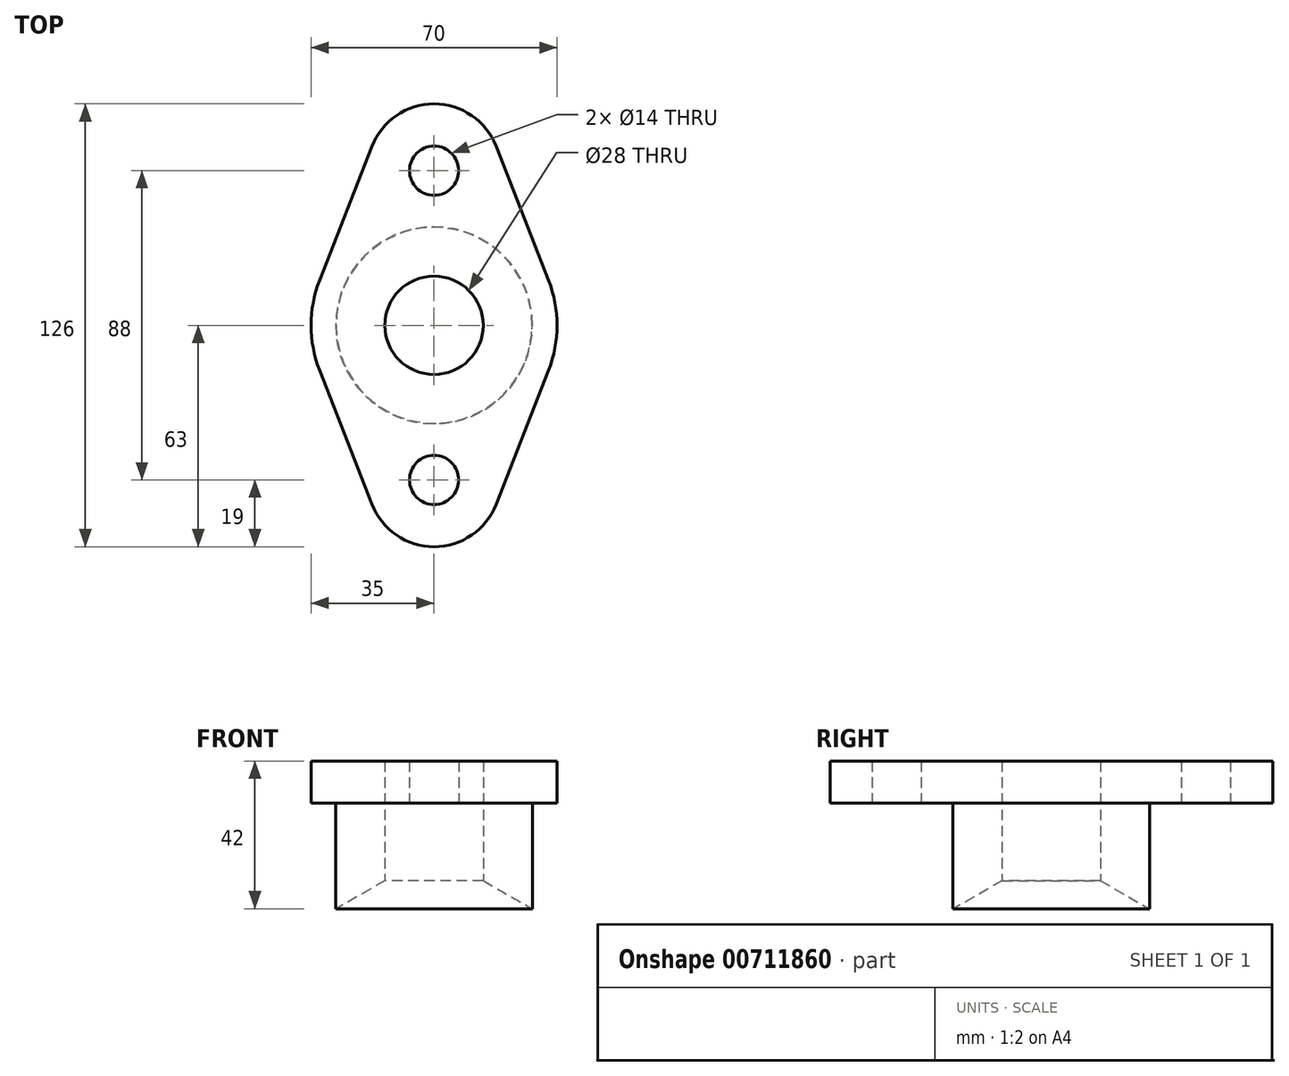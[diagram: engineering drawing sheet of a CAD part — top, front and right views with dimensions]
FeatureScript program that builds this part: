
annotation { "Feature Type Name" : "Feature", "Feature Type Description" : "" }
export const myFeature = defineFeature(function(context is Context, id is Id, definition is map)
    precondition{}
    {
        {
            var Q0;
            Q0=qCreatedBy(makeId("Top.planeOp"),FACE);
            var sketch = newSketch(context, id + "F0", { "sketchPlane" : qUnion([Q0])});
            skLineSegment(sketch, "E0", {"start": v(-35, 0) * mm, "end": v(35, 0) * mm, "construction": true});
            skLineSegment(sketch, "E1", {"start": v(0, 44) * mm, "end": v(0, -44) * mm, "construction": true});
            skCircle(sketch, "E2", {"center": v(0, 44) * mm, "radius": 7 * mm});
            skCircle(sketch, "E3", {"center": v(0, -44) * mm, "radius": 7 * mm});
            skArc(sketch, "E4", {"start": v(17.7, 50.9) * mm, "mid": v(0, 63) * mm, "end": v(-17.7, 50.9) * mm});
            skArc(sketch, "E5", {"start": v(-32.6, 12.73) * mm, "mid": v(-35, 0) * mm, "end": v(-32.6, -12.73) * mm});
            skCircle(sketch, "E6", {"center": v(0, 0) * mm, "radius": 14 * mm});
            skLineSegment(sketch, "E7", {"start": v(17.7, 50.9) * mm, "end": v(32.6, 12.73) * mm});
            skLineSegment(sketch, "E8.MirrorCS", {"start": v(-17.7, 50.9) * mm, "end": v(-32.6, 12.73) * mm});
            skLineSegment(sketch, "E9.MirrorCS", {"start": v(35, 0) * mm, "end": v(-35, 0) * mm, "construction": true});
            skLineSegment(sketch, "E10.MirrorCS", {"start": v(17.7, -50.9) * mm, "end": v(32.6, -12.73) * mm});
            skLineSegment(sketch, "E11.MirrorCS", {"start": v(-17.7, -50.9) * mm, "end": v(-32.6, -12.73) * mm});
            skArc(sketch, "E12.trimOffspring", {"start": v(32.6, -12.73) * mm, "mid": v(35, 0) * mm, "end": v(32.6, 12.73) * mm});
            skArc(sketch, "E13.trimOffspring", {"start": v(-17.7, -50.9) * mm, "mid": v(0, -63) * mm, "end": v(17.7, -50.9) * mm});
            skSolve(sketch);
        }
        {
            var Q0;
            Q0 = qSketchRegion(id + "F0", true);
            extrude(context, id + "F1", {"entities" : qUnion([Q0]), "depth" : 42 * mm, "offsetDistance" : 25 * mm});
        }
        {
            var Q0;
            Q0=makeQuery(id+"F1.opExtrude","CAP_FACE",FACE,{"disambiguationData":[OSD([sQuery(id+"F0.wireOp",EDGE,"E2"),sQuery(id+"F0.wireOp",EDGE,"E3"),sQuery(id+"F0.wireOp",EDGE,"E4"),sQuery(id+"F0.wireOp",EDGE,"E5"),sQuery(id+"F0.wireOp",EDGE,"E6"),sQuery(id+"F0.wireOp",EDGE,"E7"),sQuery(id+"F0.wireOp",EDGE,"E8.MirrorCS"),sQuery(id+"F0.wireOp",EDGE,"E10.MirrorCS"),sQuery(id+"F0.wireOp",EDGE,"E11.MirrorCS"),sQuery(id+"F0.wireOp",EDGE,"E12.trimOffspring"),sQuery(id+"F0.wireOp",EDGE,"E13.trimOffspring")])],"isStart":true});
            var sketch = newSketch(context, id + "F2", { "sketchPlane" : qUnion([Q0])});
            skCircle(sketch, "E14", {"center": v(0, 0) * mm, "radius": 28 * mm});
            skSolve(sketch);
        }
        {
            var Q0;
            Q0=makeQuery(id+"F2.imprint","IMPRINT",FACE,{"disambiguationData":[TD([[makeQuery(id+"F2.imprint","IMPRINT",EDGE,{"derivedFrom":sQuery(id+"F2.wireOp",EDGE,"E14")}),-1.0]])]});
            extrude(context, id + "F3", {"entities" : qUnion([Q0]), "operationType" : NewBodyOperationType.REMOVE, "oppositeDirection" : true, "depth" : 30 * mm, "offsetDistance" : 25 * mm});
        }
        {
            var Q0;
            Q0=makeQuery(id+"F1.opExtrude","CAP_EDGE",EDGE,{"disambiguationData":[OSD([sQuery(id+"F0.wireOp",EDGE,"E6")])],"isStart":true});
            chamfer(context, id + "F4", {"entities" : qUnion([Q0]), "chamferType" : ChamferType.OFFSET_ANGLE, "width" : 8 * mm, "oppositeDirection" : true, "angle" : 60 * degree, "tangentPropagation" : true});
        }
    });
